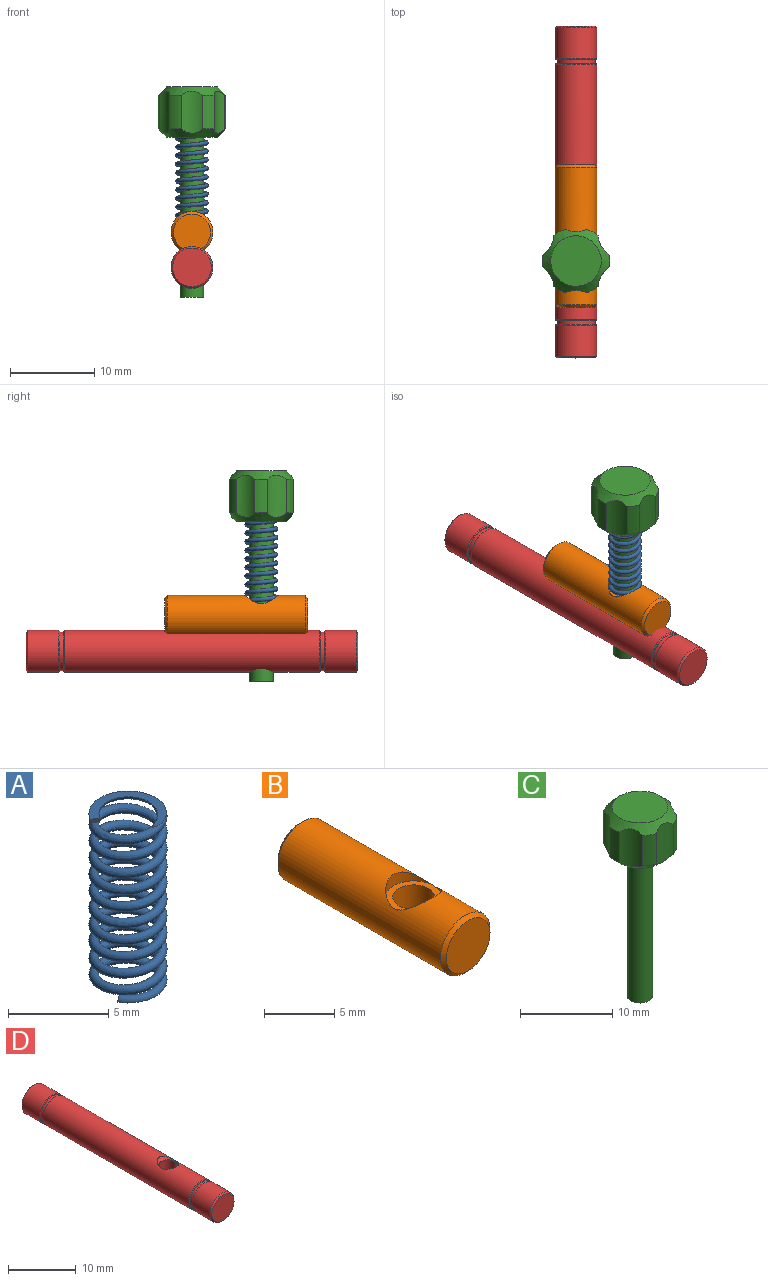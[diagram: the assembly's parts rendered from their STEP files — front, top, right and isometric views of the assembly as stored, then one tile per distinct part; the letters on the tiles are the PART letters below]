
ASSEMBLY  parts=4 mates=3
PART A: 7 faces, bbox 4.1x4.5x11.2 mm
  f0: bspline ~11.2x4.5mm, area 165.1mm2, adj f1,f3,f5,f6
  f1: torus R=1.7mm, axis (0,0,-1), area 3.5mm2, adj f0,f2,f6
  f2: plane 0.43x0.25mm, normal (-0.5,-0.87,0), area 0.1mm2, adj f1,f6
  f3: torus R=1.7mm, axis (0,0,1), area 3.5mm2, adj f0,f4,f5
  f4: plane 0.43x0.25mm, normal (-0.5,0.87,0), area 0.1mm2, adj f3,f5
  f5: plane 3.73x3.64mm, normal (0,0,-1), area 3.3mm2, adj f0,f3,f4
  f6: plane 3.73x3.64mm, normal (0,0,1), area 3.4mm2, adj f0,f1,f2
PART B: 9 faces, bbox 5x17x5 mm
  f0: cylinder r=1.5mm len=4mm, axis (0,0,1), area 35.4mm2, adj f1,f8
  f1: cylinder r=2.5mm len=16.4mm, axis (0,1,0), area 236.2mm2, adj f0,f4,f5,f6,f7
  f2: plane 4.4x4.4mm, normal (0,-1,0), area 15.2mm2, adj f5
  f3: plane 4.4x4.4mm, normal (0,1,0), area 15.2mm2, adj f4
  f4: cone r=2.5mm half-angle=45deg, axis (0,-1,0), area 6.3mm2, adj f1,f3
  f5: cone r=2.2mm half-angle=45deg, axis (0,1,0), area 6.3mm2, adj f1,f2
  f6: cylinder r=2mm len=4mm, axis (0,0,1), area 3.3mm2, adj f1,f8
  f7: cylinder r=2mm len=4mm, axis (0,0,1), area 3.3mm2, adj f1,f8
  f8: plane 4x4mm, normal (0,0,1), area 5.5mm2, adj f0,f6,f7
PART C: 18 faces, bbox 8x8x25 mm
  f0: cylinder r=4mm len=4mm, axis (0,0,-1), area 6.3mm2, adj f5,f6,f10,f15
  f1: cylinder r=4mm len=4mm, axis (0,0,-1), area 6.3mm2, adj f5,f6,f13,f14
  f2: cylinder r=4mm len=4mm, axis (0,0,-1), area 6.3mm2, adj f5,f6,f12,f13
  f3: cylinder r=4mm len=4mm, axis (0,0,-1), area 6.3mm2, adj f5,f6,f11,f12
  f4: cylinder r=4mm len=4mm, axis (0,0,-1), area 6.3mm2, adj f5,f6,f11,f15
  f5: cone r=4mm half-angle=45deg, axis (0,0,1), area 23.8mm2, adj f0,f1,f2,f3,f4,f7,f9,f10
  f6: cone r=3mm half-angle=45deg, axis (0,0,-1), area 23.8mm2, adj f0,f1,f2,f3,f4,f7,f8,f10
  f7: cylinder r=4mm len=4mm, axis (0,0,-1), area 6.3mm2, adj f5,f6,f10,f14
  f8: plane 6x6mm, normal (0,0,1), area 28.3mm2, adj f6
  f9: plane 6x6mm, normal (0,0,-1), area 22.1mm2, adj f5,f16
  f10: cylinder r=3mm len=5mm, axis (0,0,-1), area 12.3mm2, adj f0,f5,f6,f7
  f11: cylinder r=3mm len=5mm, axis (0,0,-1), area 12.3mm2, adj f3,f4,f5,f6
  f12: cylinder r=3mm len=5mm, axis (0,0,-1), area 12.3mm2, adj f2,f3,f5,f6
  f13: cylinder r=3mm len=5mm, axis (0,0,-1), area 12.3mm2, adj f1,f2,f5,f6
  f14: cylinder r=3mm len=5mm, axis (0,0,-1), area 12.3mm2, adj f1,f5,f6,f7
  f15: cylinder r=3mm len=5mm, axis (0,0,-1), area 12.3mm2, adj f0,f4,f5,f6
  f16: cylinder r=1.4mm len=19mm, axis (0,0,1), area 167.1mm2, adj f9,f17
  f17: plane 2.8x2.8mm, normal (0,0,-1), area 6.2mm2, adj f16
PART D: 19 faces, bbox 5x39.5x5 mm
  f0: cylinder r=2.5mm len=30.3mm, axis (0,1,0), area 463.1mm2, adj f1,f2,f16,f17
  f1: cylinder r=1.25mm len=4.5mm, axis (0,0,1), area 34.1mm2, adj f0,f2
  f2: cone r=1.25mm half-angle=45deg, axis (0,0,1), area 3.6mm2, adj f0,f1
  f3: cylinder r=2.3mm len=4.6mm, axis (0,1,0), area 7.2mm2, adj f4,f5
  f4: plane 4.8x4.8mm, normal (0,1,0), area 1.5mm2, adj f3,f17
  f5: plane 4.8x4.8mm, normal (0,-1,0), area 1.5mm2, adj f3,f18
  f6: plane 4.6x4.6mm, normal (0,1,0), area 16.6mm2, adj f13
  f7: cylinder r=2.5mm len=5mm, axis (0,1,0), area 58.1mm2, adj f13,f18
  f8: cylinder r=2.3mm len=4.6mm, axis (0,-1,0), area 7.2mm2, adj f9,f10
  f9: plane 4.8x4.8mm, normal (0,-1,0), area 1.5mm2, adj f8,f16
  f10: plane 4.8x4.8mm, normal (0,1,0), area 1.5mm2, adj f8,f15
  f11: plane 4.6x4.6mm, normal (0,-1,0), area 16.6mm2, adj f14
  f12: cylinder r=2.5mm len=5mm, axis (0,1,0), area 58.1mm2, adj f14,f15
  f13: cone r=2.5mm half-angle=45deg, axis (0,-1,0), area 4.3mm2, adj f6,f7
  f14: cone r=2.3mm half-angle=45deg, axis (0,1,0), area 4.3mm2, adj f11,f12
  f15: cone r=2.5mm half-angle=45deg, axis (0,-1,0), area 2.2mm2, adj f10,f12
  f16: cone r=2.4mm half-angle=45deg, axis (0,1,0), area 2.2mm2, adj f0,f9
  f17: cone r=2.5mm half-angle=45deg, axis (0,-1,0), area 2.2mm2, adj f0,f4
  f18: cone r=2.4mm half-angle=45deg, axis (0,1,0), area 2.2mm2, adj f5,f7
PLACE A t=(16,1,22.66)mm
PLACE B t=(16,12.5,21.16)mm
PLACE C t=(16,1,32.47)mm
PLACE D t=(16,29,17)mm
MATE fastened A.f1 <-> B.f0  axis (0,0,-1) through (16,1,22.66)mm
MATE slider C.f0 <-> B.f0  axis (0,0,1) through (16,1,22.97)mm
MATE fastened C.f0 <-> D.f1  axis (0,0,-1) through (16,1,13.47)mm
